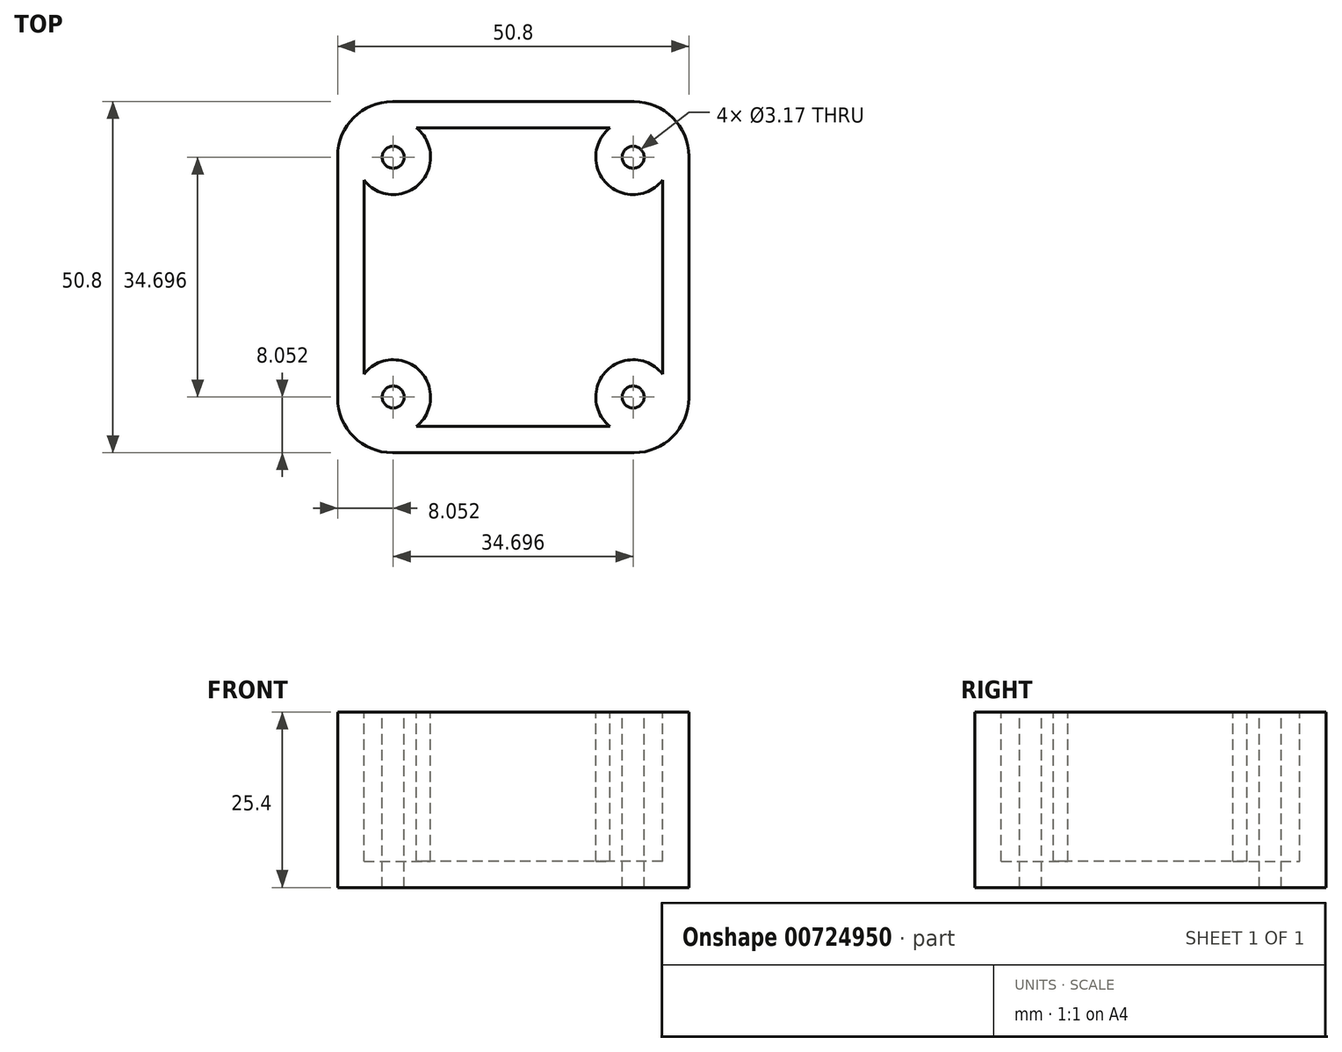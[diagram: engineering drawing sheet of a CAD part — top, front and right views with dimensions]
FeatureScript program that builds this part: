
annotation { "Feature Type Name" : "Feature", "Feature Type Description" : "" }
export const myFeature = defineFeature(function(context is Context, id is Id, definition is map)
    precondition{}
    {
        {
            var Q0;
            Q0=qCreatedBy(makeId("Top.planeOp"),FACE);
            var sketch = newSketch(context, id + "F0", { "sketchPlane" : qUnion([Q0])});
            skLineSegment(sketch, "E0.bottom", {"start": v(25.4, 25.4) * mm, "end": v(-25.4, 25.4) * mm});
            skLineSegment(sketch, "E0.top", {"start": v(25.4, -25.4) * mm, "end": v(-25.4, -25.4) * mm});
            skLineSegment(sketch, "E0.left", {"start": v(25.4, 25.4) * mm, "end": v(25.4, -25.4) * mm});
            skLineSegment(sketch, "E0.right", {"start": v(-25.4, 25.4) * mm, "end": v(-25.4, -25.4) * mm});
            skPoint(sketch, "E0.middle", {"position": v(0, 0) * mm});
            skSolve(sketch);
        }
        {
            var Q0;
            Q0 = qSketchRegion(id + "F0", true);
            extrude(context, id + "F1", {"entities" : qUnion([Q0]), "depth" : 25.4 * mm, "offsetDistance" : 25.4 * mm});
        }
        {
            var Q0;
            Q0=makeQuery(id+"F1.opExtrude","CAP_FACE",FACE,{"disambiguationData":[OSD([sQuery(id+"F0.wireOp",EDGE,"E0.bottom"),sQuery(id+"F0.wireOp",EDGE,"E0.top"),sQuery(id+"F0.wireOp",EDGE,"E0.left"),sQuery(id+"F0.wireOp",EDGE,"E0.right")])],"isStart":false});
            var sketch = newSketch(context, id + "F2", { "sketchPlane" : qUnion([Q0])});
            skCircle(sketch, "E1", {"center": v(17.35, 17.35) * mm, "radius": 1.59 * mm});
            skCircle(sketch, "E2.MirrorC", {"center": v(17.35, -17.35) * mm, "radius": 1.59 * mm});
            skCircle(sketch, "E3.MirrorC", {"center": v(-17.35, 17.35) * mm, "radius": 1.59 * mm});
            skCircle(sketch, "E4.MirrorC", {"center": v(-17.35, -17.35) * mm, "radius": 1.59 * mm});
            skSolve(sketch);
        }
        {
            var Q0;
            Q0 = qSketchRegion(id + "F2", true);
            extrude(context, id + "F3", {"entities" : qUnion([Q0]), "operationType" : NewBodyOperationType.REMOVE, "endBound" : BoundingType.UP_TO_NEXT, "oppositeDirection" : true, "depth" : 25.4 * mm, "offsetDistance" : 25.4 * mm});
        }
        {
            var Q0;
            Q0=makeQuery(id+"F1.opExtrude","SWEPT_EDGE",EDGE,{"disambiguationData":[OSD([sQuery(id+"F0.wireOp",EDGE,"E0.top"),sQuery(id+"F0.wireOp",EDGE,"E0.left")])]});
            var Q1;
            Q1=makeQuery(id+"F1.opExtrude","SWEPT_EDGE",EDGE,{"disambiguationData":[OSD([sQuery(id+"F0.wireOp",EDGE,"E0.bottom"),sQuery(id+"F0.wireOp",EDGE,"E0.left")])]});
            var Q2;
            Q2=makeQuery(id+"F1.opExtrude","SWEPT_EDGE",EDGE,{"disambiguationData":[OSD([sQuery(id+"F0.wireOp",EDGE,"E0.top"),sQuery(id+"F0.wireOp",EDGE,"E0.right")])]});
            var Q3;
            Q3=makeQuery(id+"F1.opExtrude","SWEPT_EDGE",EDGE,{"disambiguationData":[OSD([sQuery(id+"F0.wireOp",EDGE,"E0.bottom"),sQuery(id+"F0.wireOp",EDGE,"E0.right")])]});
            fillet(context, id + "F4", {"entities" : qUnion([Q0, Q1, Q2, Q3]), "radius" : 7.94 * mm, "tangentPropagation" : true, "allowEdgeOverflow" : false});
        }
        {
            var Q0;
            Q0=makeQuery(id+"F1.opExtrude","CAP_FACE",FACE,{"disambiguationData":[OSD([sQuery(id+"F0.wireOp",EDGE,"E0.bottom"),sQuery(id+"F0.wireOp",EDGE,"E0.top"),sQuery(id+"F0.wireOp",EDGE,"E0.left"),sQuery(id+"F0.wireOp",EDGE,"E0.right")])],"isStart":false});
            shell(context, id + "F5", {"entities" : qUnion([Q0]), "thickness" : 3.8 * mm});
        }
    });
